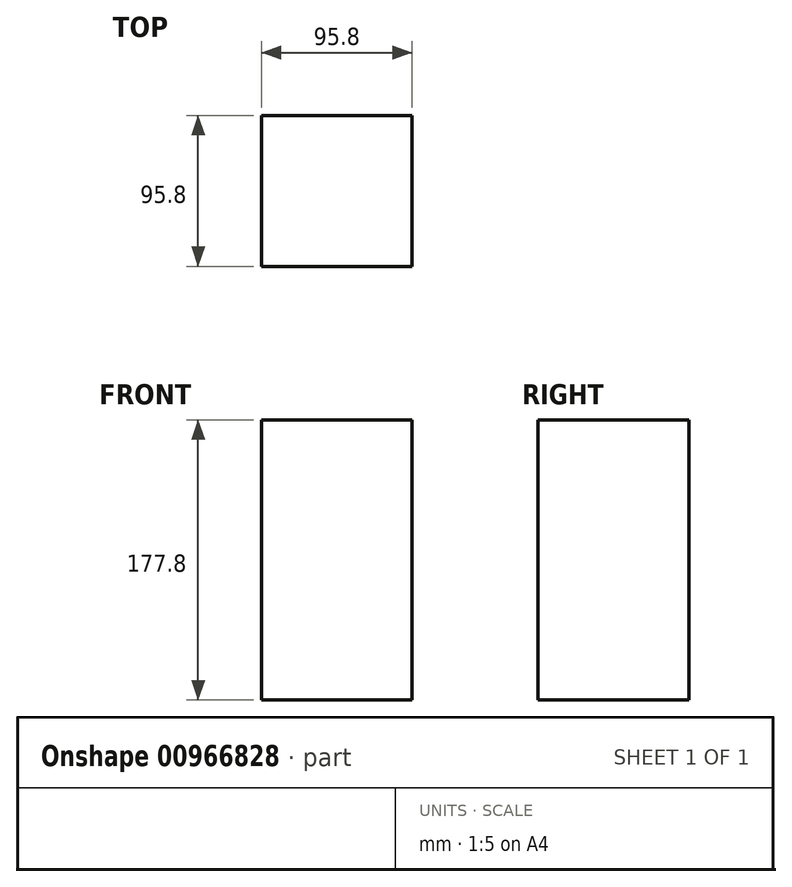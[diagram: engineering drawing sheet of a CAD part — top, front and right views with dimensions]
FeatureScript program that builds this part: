
annotation { "Feature Type Name" : "Feature", "Feature Type Description" : "" }
export const myFeature = defineFeature(function(context is Context, id is Id, definition is map)
    precondition{}
    {
        {
            var Q0;
            Q0=qCreatedBy(makeId("Top.planeOp"),FACE);
            var sketch = newSketch(context, id + "F0", { "sketchPlane" : qUnion([Q0])});
            skLineSegment(sketch, "E0.bottom", {"start": v(-47.9, 47.9) * mm, "end": v(47.9, 47.9) * mm});
            skLineSegment(sketch, "E0.top", {"start": v(-47.9, -47.9) * mm, "end": v(47.9, -47.9) * mm});
            skLineSegment(sketch, "E0.left", {"start": v(-47.9, 47.9) * mm, "end": v(-47.9, -47.9) * mm});
            skLineSegment(sketch, "E0.right", {"start": v(47.9, 47.9) * mm, "end": v(47.9, -47.9) * mm});
            skSolve(sketch);
        }
        {
            var Q0;
            Q0 = qSketchRegion(id + "F0", true);
            extrude(context, id + "F1", {"entities" : qUnion([Q0]), "endBound" : BoundingType.SYMMETRIC, "depth" : 177.8 * mm, "offsetDistance" : 25 * mm});
        }
    });
